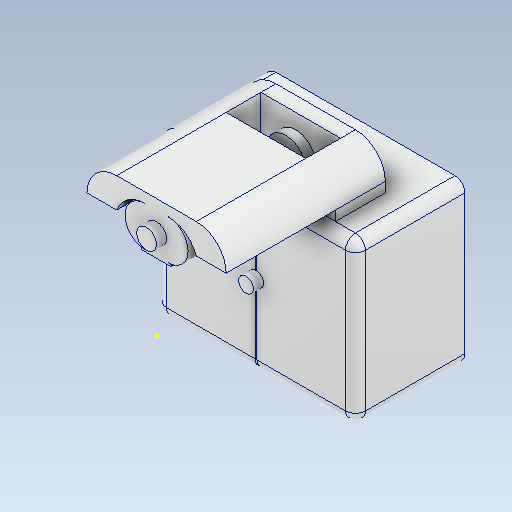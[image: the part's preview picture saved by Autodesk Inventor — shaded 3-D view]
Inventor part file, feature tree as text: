
AUTODESK INVENTOR PART (.ipt)
format: ipt  version: 2021 (Build 250183000, 183)  size: 326,144 bytes
history: native  units: mm
features: sketch x27, other x3, plane x2
ambient origin geometry x8: Origin, YZ Plane, XZ Plane, XY Plane, X Axis, Y Axis, Z Axis, Center Point
bodies: Solid1 (feature_tree)
feature tree (32):
  other  "Gear and handle.ipt"
  other  "Solid1::Gear and handle.ipt"
  other  "TaggingFeature1"
  sketch  "Sketch1"  dims[d0=10.0mm]
  sketch  "Sketch2"
  sketch  "Sketch3"
  sketch  "Sketch4"
  sketch  "Sketch5"
  sketch  "Sketch6"
  sketch  "Sketch7"
  sketch  "Sketch8"
  sketch  "Sketch9"
  sketch  "Sketch10"
  sketch  "Sketch11"
  sketch  "Sketch12"
  sketch  "Sketch14"
  sketch  "Sketch15"
  sketch  "Sketch16"
  sketch  "Sketch17"
  sketch  "Sketch18"
  sketch  "Sketch19"
  sketch  "Sketch24"
  sketch  "Sketch25"
  sketch  "Sketch26"
  sketch  "Sketch29"
  sketch  "Sketch30"
  sketch  "Sketch31"
  sketch  "Sketch32"
  sketch  "Sketch33"
  sketch  "Sketch34"
  plane  "Work Plane1"
  plane  "Work Plane2"
